# Revit family: Hager-GOLF-Flush_mounted-IP40-With_Cover-With_DIN-Hosted-ES-es
name_source: partatom
category: Electrical Equipment
units: mm (PartAtom-declared; Revit-internal decimal feet)

## family parameters
Cut with Voids When Loaded = No
Host = Face
Maintain Annotation Orientation = Yes
Panel Configuration = Two Columns, Circuits Across
Part Type = Panelboard
Room Calculation Point = No
Round Connector Dimension = Use Diameter
Shared = No

## types (69) — shared parameters
BC_MODEL_ID = 1539129
BC_OBJECT_ID = 512266
BC_OBJECT_VERSION = #7
Code hager = ADD-EC000214_EU
EF000003 - Método de montaje = Montado empotrado (escayola)
EF000007 - Color = Blanco
EF000024 - Resistente a UV = No
EF000049 - Profundidad = 97 mm  [stored 0.318241 ft]
EF000116 - Número RAL = 9010
EF000118 - Con placa de montaje = No
EF000218 - Profundidad de instalación = 72 mm  [stored 0.23622 ft]
EF001062 - Versión de CEM = No
EF001134 - Carril DIN = Yes
EF004462 - Tipo de cierre = Otros
EF005474 - Grado de protección (IP) = IP40
EF006306 - Con candado = No
EF009212 - Versión de la cubierta = Cerrado
ETIM class code = EC000214
ETIM class name = Small distribution board
HG000001 - Número de columnas = 1
HG000002-with door or cover-es = Yes
HG000003-Range-es = GOLF
HG000005-Thickness-es = 2 mm  [stored 0.00656168 ft]
HG000006-Flush mounted-es = Yes
HG000009-Double swing door-es = No
HG000010-Asymmetric doors-es = No
HG000011-Empty rows from bottom-es = No
HG000012-Door swing angle-es = 90.00°
HG000013-Door on the left-es = No
HG000014-Door on the right-es = Yes
HG000015-Clearance visibility-es = Yes
HG000016-Door 3D visibility-es = Yes
HG000017-Distance between poles-es = 18 mm  [stored 0.0590551 ft]
HG000060-RAL-number = 9010
HG000099-Onfly Template ID-es-ES = 507532
Manufacturer = Hager
Name = GOLF-Flush_mounted-IP40-With_Cover-With_DIN-ES
Name BIM&CO = Electricity
Name hager = ADD_Enclosures_EC000214
Uniformat = Low Tension Service & Dist.
Uniformat code = D501001
zero-valued in all types: Default Elevation, EF001131 - Profundidad interna, HG000007-Number of empty columns-es, HG000008-Number of empty rows-es

## per-type parameters (varying)
| type | BC_VARIANT_ID | EF000008 - Anchura | EF000040 - Altura | EF000266 - Número de filas | EF000332 - Altura de la instalación | EF000846 - Anchura de montaje | EF001088 - Posibilidad de extensión | EF002950 - Ancho en número de espacios modulares | EF006244 - Tapa/puerta transparente | EF015776 - Borne de tierra | EF015777 - Borne neutro | EF015941 - Puerta de transmisión de señal | HG000004-Manufacturer reference-es | HGEF000266-Número de filas | HGEF0002950-Ancho en número de espacios modulares |
| GOLF-Flush_mounted_W204_H225_D97_4_Modular_Spacing-VF104PE | 1169244 | 204 mm | 225 mm  [stored 0.738189 ft] | 1 | 189 mm  [stored 0.620079 ft] | 170 mm  [stored 0.557743 ft] | Yes | 4 | No | Yes | No | Yes | VF104PE | 1 | 4 |
| GOLF-Flush_mounted_W204_H225_D97_4_Modular_Spacing-VF104PEH | 1169258 | 204 mm | 225 mm  [stored 0.738189 ft] | 1 | 189 mm  [stored 0.620079 ft] | 170 mm  [stored 0.557743 ft] | Yes | 4 | No | Yes | No | Yes | VF104PEH | 1 | 4 |
| GOLF-Flush_mounted_W204_H225_D97_4_Modular_Spacing-VF104TE | 1169267 | 204 mm | 225 mm  [stored 0.738189 ft] | 1 | 189 mm  [stored 0.620079 ft] | 170 mm  [stored 0.557743 ft] | Yes | 4 | Yes | Yes | No | Yes | VF104TE | 1 | 4 |
| GOLF-Flush_mounted_W275_H225_D97_8_Modular_Spacing-VF108PE | 1169271 | 275 mm | 225 mm  [stored 0.738189 ft] | 1 | 189 mm  [stored 0.620079 ft] | 242 mm  [stored 0.793963 ft] | Yes | 8 | No | Yes | No | Yes | VF108PE | 1 | 8 |
| GOLF-Flush_mounted_W275_H225_D97_8_Modular_Spacing-VF108PEH | 1169277 | 275 mm | 225 mm  [stored 0.738189 ft] | 1 | 189 mm  [stored 0.620079 ft] | 242 mm  [stored 0.793963 ft] | Yes | 8 | No | Yes | No | Yes | VF108PEH | 1 | 8 |
| GOLF-Flush_mounted_W275_H225_D97_8_Modular_Spacing-VF108TE | 1169281 | 275 mm | 225 mm  [stored 0.738189 ft] | 1 | 189 mm  [stored 0.620079 ft] | 242 mm  [stored 0.793963 ft] | Yes | 8 | Yes | Yes | No | Yes | VF108TE | 1 | 8 |
| GOLF-Flush_mounted_W275_H225_D97_8_Modular_Spacing-VF108TJ | 1169285 | 275 mm | 225 mm  [stored 0.738189 ft] | 1 | 189 mm  [stored 0.620079 ft] | 242 mm  [stored 0.793963 ft] | Yes | 8 | Yes | Yes | Yes | Yes | VF108TJ | 1 | 8 |
| GOLF-Flush_mounted_W352_H293_D97_12_Modular_Spacing-VF112PE | 1169289 | 352 mm  [stored 1.15486 ft] | 293 mm | 1 | 257 mm  [stored 0.843176 ft] | 318 mm  [stored 1.04331 ft] | Yes | 12 | No | Yes | No | Yes | VF112PE | 1 | 12 |
| GOLF-Flush_mounted_W352_H293_D97_12_Modular_Spacing-VF112PEH | 1169292 | 352 mm  [stored 1.15486 ft] | 293 mm | 1 | 257 mm  [stored 0.843176 ft] | 318 mm  [stored 1.04331 ft] | Yes | 12 | No | Yes | No | Yes | VF112PEH | 1 | 12 |
| GOLF-Flush_mounted_W352_H293_D97_12_Modular_Spacing-VF112PJ | 1169296 | 352 mm  [stored 1.15486 ft] | 293 mm | 1 | 257 mm  [stored 0.843176 ft] | 318 mm  [stored 1.04331 ft] | Yes | 12 | No | Yes | Yes | Yes | VF112PJ | 1 | 12 |
| GOLF-Flush_mounted_W352_H293_D97_12_Modular_Spacing-VF112PY | 1169299 | 352 mm  [stored 1.15486 ft] | 293 mm | 1 | 257 mm  [stored 0.843176 ft] | 318 mm  [stored 1.04331 ft] | Yes | 12 | No | No | No | No | VF112PY | 1 | 12 |
| GOLF-Flush_mounted_W352_H293_D97_12_Modular_Spacing-VF112TE | 1169302 | 352 mm  [stored 1.15486 ft] | 293 mm | 1 | 257 mm  [stored 0.843176 ft] | 318 mm  [stored 1.04331 ft] | Yes | 12 | Yes | Yes | No | Yes | VF112TE | 1 | 12 |
| GOLF-Flush_mounted_W352_H293_D97_12_Modular_Spacing-VF112TF | 1169305 | 352 mm  [stored 1.15486 ft] | 293 mm | 1 | 257 mm  [stored 0.843176 ft] | 318 mm  [stored 1.04331 ft] | Yes | 12 | Yes | Yes | No | Yes | VF112TF | 1 | 12 |
| GOLF-Flush_mounted_W352_H293_D97_12_Modular_Spacing-VF112TJ | 1169308 | 352 mm  [stored 1.15486 ft] | 293 mm | 1 | 257 mm  [stored 0.843176 ft] | 318 mm  [stored 1.04331 ft] | Yes | 12 | Yes | Yes | Yes | Yes | VF112TJ | 1 | 12 |
| GOLF-Flush_mounted_W352_H293_D97_12_Modular_Spacing-VF112TY | 1169310 | 352 mm  [stored 1.15486 ft] | 293 mm | 1 | 257 mm  [stored 0.843176 ft] | 318 mm  [stored 1.04331 ft] | Yes | 12 | Yes | Yes | Yes | Yes | VF112TY | 1 | 12 |
| GOLF-Flush_mounted_W460_H293_D97_18_Modular_Spacing-VF118PEH | 1169312 | 460 mm  [stored 1.50919 ft] | 293 mm | 1 | 257 mm  [stored 0.843176 ft] | 426 mm  [stored 1.39764 ft] | Yes | 18 | No | Yes | No | Yes | VF118PEH | 1 | 18 |
| GOLF-Flush_mounted_W460_H293_D97_18_Modular_Spacing-VF118PES | 1169314 | 460 mm  [stored 1.50919 ft] | 293 mm | 1 | 257 mm  [stored 0.843176 ft] | 426 mm  [stored 1.39764 ft] | Yes | 18 | No | No | No | Yes | VF118PES | 1 | 18 |
| GOLF-Flush_mounted_W460_H293_D97_18_Modular_Spacing-VF118PJ | 1169316 | 460 mm  [stored 1.50919 ft] | 293 mm | 1 | 257 mm  [stored 0.843176 ft] | 426 mm  [stored 1.39764 ft] | Yes | 18 | No | Yes | Yes | Yes | VF118PJ | 1 | 18 |
| GOLF-Flush_mounted_W460_H293_D97_18_Modular_Spacing-VF118PY | 1169318 | 460 mm  [stored 1.50919 ft] | 293 mm | 1 | 257 mm  [stored 0.843176 ft] | 426 mm  [stored 1.39764 ft] | Yes | 18 | No | Yes | Yes | Yes | VF118PY | 1 | 18 |
| GOLF-Flush_mounted_W460_H293_D97_18_Modular_Spacing-VF118TES | 1169320 | 460 mm  [stored 1.50919 ft] | 293 mm | 1 | 257 mm  [stored 0.843176 ft] | 426 mm  [stored 1.39764 ft] | Yes | 18 | Yes | No | No | Yes | VF118TES | 1 | 18 |
| GOLF-Flush_mounted_W460_H293_D97_18_Modular_Spacing-VF118TF | 1169322 | 460 mm  [stored 1.50919 ft] | 293 mm | 1 | 257 mm  [stored 0.843176 ft] | 426 mm  [stored 1.39764 ft] | Yes | 18 | Yes | Yes | No | Yes | VF118TF | 1 | 18 |
| GOLF-Flush_mounted_W460_H293_D97_18_Modular_Spacing-VF118TJ | 1169324 | 460 mm  [stored 1.50919 ft] | 293 mm | 1 | 257 mm  [stored 0.843176 ft] | 426 mm  [stored 1.39764 ft] | Yes | 18 | Yes | Yes | Yes | Yes | VF118TJ | 1 | 18 |
| GOLF-Flush_mounted_W532_H293_D97_22_Modular_Spacing-VF122PJ | 1169326 | 532 mm  [stored 1.74541 ft] | 293 mm | 1 | 257 mm  [stored 0.843176 ft] | 498 mm  [stored 1.63386 ft] | Yes | 22 | No | Yes | Yes | Yes | VF122PJ | 1 | 22 |
| GOLF-Flush_mounted_W532_H293_D97_22_Modular_Spacing-VF122PY | 1169328 | 532 mm  [stored 1.74541 ft] | 293 mm | 1 | 257 mm  [stored 0.843176 ft] | 498 mm  [stored 1.63386 ft] | Yes | 22 | No | Yes | Yes | Yes | VF122PY | 1 | 22 |
| GOLF-Flush_mounted_W532_H293_D97_22_Modular_Spacing-VF122TJ | 1169330 | 532 mm  [stored 1.74541 ft] | 293 mm | 1 | 257 mm  [stored 0.843176 ft] | 498 mm  [stored 1.63386 ft] | Yes | 22 | Yes | Yes | Yes | Yes | VF122TJ | 1 | 22 |
| GOLF-Flush_mounted_W382_H418_D97_12_Modular_Spacing-VF212PE | 1169332 | 382 mm  [stored 1.25328 ft] | 418 mm  [stored 1.37139 ft] | 2 | 382 mm  [stored 1.25328 ft] | 318 mm  [stored 1.04331 ft] | Yes | 12 | No | Yes | No | Yes | VF212PE | 2 | 12 |
| GOLF-Flush_mounted_W382_H418_D97_12_Modular_Spacing-VF212PEH | 1169333 | 382 mm  [stored 1.25328 ft] | 418 mm  [stored 1.37139 ft] | 2 | 382 mm  [stored 1.25328 ft] | 318 mm  [stored 1.04331 ft] | Yes | 12 | No | Yes | No | Yes | VF212PEH | 2 | 12 |
| GOLF-Flush_mounted_W382_H418_D97_12_Modular_Spacing-VF212PJ | 1169335 | 382 mm  [stored 1.25328 ft] | 418 mm  [stored 1.37139 ft] | 2 | 382 mm  [stored 1.25328 ft] | 318 mm  [stored 1.04331 ft] | Yes | 12 | No | Yes | Yes | Yes | VF212PJ | 2 | 12 |
| GOLF-Flush_mounted_W382_H418_D97_12_Modular_Spacing-VF212PY | 1169337 | 382 mm  [stored 1.25328 ft] | 418 mm  [stored 1.37139 ft] | 2 | 382 mm  [stored 1.25328 ft] | 318 mm  [stored 1.04331 ft] | Yes | 12 | No | Yes | Yes | Yes | VF212PY | 2 | 12 |
| GOLF-Flush_mounted_W382_H418_D97_12_Modular_Spacing-VF212TE | 1169339 | 382 mm  [stored 1.25328 ft] | 418 mm  [stored 1.37139 ft] | 2 | 382 mm  [stored 1.25328 ft] | 318 mm  [stored 1.04331 ft] | Yes | 12 | Yes | Yes | No | Yes | VF212TE | 2 | 12 |
| GOLF-Flush_mounted_W382_H418_D97_12_Modular_Spacing-VF212TF | 1169341 | 382 mm  [stored 1.25328 ft] | 418 mm  [stored 1.37139 ft] | 2 | 382 mm  [stored 1.25328 ft] | 318 mm  [stored 1.04331 ft] | Yes | 12 | Yes | Yes | No | Yes | VF212TF | 2 | 12 |
| GOLF-Flush_mounted_W382_H418_D97_12_Modular_Spacing-VF212TJ | 1169342 | 382 mm  [stored 1.25328 ft] | 418 mm  [stored 1.37139 ft] | 2 | 382 mm  [stored 1.25328 ft] | 318 mm  [stored 1.04331 ft] | Yes | 12 | Yes | Yes | Yes | Yes | VF212TJ | 2 | 12 |
| GOLF-Flush_mounted_W382_H418_D97_12_Modular_Spacing-VF212TY | 1169344 | 382 mm  [stored 1.25328 ft] | 418 mm  [stored 1.37139 ft] | 2 | 382 mm  [stored 1.25328 ft] | 318 mm  [stored 1.04331 ft] | Yes | 12 | Yes | Yes | Yes | Yes | VF212TY | 2 | 12 |
| GOLF-Flush_mounted_W460_H418_D97_18_Modular_Spacing-VF218PEH | 1169346 | 460 mm  [stored 1.50919 ft] | 418 mm  [stored 1.37139 ft] | 2 | 382 mm  [stored 1.25328 ft] | 426 mm  [stored 1.39764 ft] | Yes | 18 | No | Yes | No | Yes | VF218PEH | 2 | 18 |
| GOLF-Flush_mounted_W460_H418_D97_18_Modular_Spacing-VF218PES | 1169347 | 460 mm  [stored 1.50919 ft] | 418 mm  [stored 1.37139 ft] | 2 | 382 mm  [stored 1.25328 ft] | 426 mm  [stored 1.39764 ft] | Yes | 18 | No | No | No | Yes | VF218PES | 2 | 18 |
| GOLF-Flush_mounted_W460_H418_D97_18_Modular_Spacing-VF218PF | 1169348 | 460 mm  [stored 1.50919 ft] | 418 mm  [stored 1.37139 ft] | 2 | 382 mm  [stored 1.25328 ft] | 426 mm  [stored 1.39764 ft] | Yes | 18 | No | Yes | No | Yes | VF218PF | 2 | 18 |
| GOLF-Flush_mounted_W460_H418_D97_18_Modular_Spacing-VF218PJ | 1169349 | 460 mm  [stored 1.50919 ft] | 418 mm  [stored 1.37139 ft] | 2 | 382 mm  [stored 1.25328 ft] | 426 mm  [stored 1.39764 ft] | Yes | 18 | No | Yes | Yes | Yes | VF218PJ | 2 | 18 |
| GOLF-Flush_mounted_W460_H418_D97_18_Modular_Spacing-VF218PY | 1169350 | 460 mm  [stored 1.50919 ft] | 418 mm  [stored 1.37139 ft] | 2 | 382 mm  [stored 1.25328 ft] | 426 mm  [stored 1.39764 ft] | Yes | 18 | No | Yes | Yes | Yes | VF218PY | 2 | 18 |
| GOLF-Flush_mounted_W460_H418_D97_18_Modular_Spacing-VF218TES | 1169351 | 460 mm  [stored 1.50919 ft] | 418 mm  [stored 1.37139 ft] | 2 | 382 mm  [stored 1.25328 ft] | 426 mm  [stored 1.39764 ft] | Yes | 18 | Yes | No | No | Yes | VF218TES | 2 | 18 |
| GOLF-Flush_mounted_W460_H418_D97_18_Modular_Spacing-VF218TF | 1169352 | 460 mm  [stored 1.50919 ft] | 418 mm  [stored 1.37139 ft] | 2 | 382 mm  [stored 1.25328 ft] | 426 mm  [stored 1.39764 ft] | No | 18 | No | No | No | No | VF218TF | 2 | 18 |
| GOLF-Flush_mounted_W460_H418_D97_18_Modular_Spacing-VF218TJ | 1169353 | 460 mm  [stored 1.50919 ft] | 418 mm  [stored 1.37139 ft] | 2 | 382 mm  [stored 1.25328 ft] | 426 mm  [stored 1.39764 ft] | Yes | 18 | Yes | Yes | Yes | Yes | VF218TJ | 2 | 18 |
| GOLF-Flush_mounted_W352_H543_D97_12_Modular_Spacing-VF312ICT | 1169354 | 352 mm  [stored 1.15486 ft] | 543 mm  [stored 1.7815 ft] | 3 | 507 mm  [stored 1.66339 ft] | 318 mm  [stored 1.04331 ft] | Yes | 12 | No | No | No | Yes | VF312ICT | 3 | 12 |
| GOLF-Flush_mounted_W352_H543_D97_12_Modular_Spacing-VF312PE | 1169355 | 352 mm  [stored 1.15486 ft] | 543 mm  [stored 1.7815 ft] | 3 | 507 mm  [stored 1.66339 ft] | 318 mm  [stored 1.04331 ft] | Yes | 12 | No | Yes | No | Yes | VF312PE | 3 | 12 |
| GOLF-Flush_mounted_W352_H543_D97_12_Modular_Spacing-VF312PEH | 1169356 | 352 mm  [stored 1.15486 ft] | 543 mm  [stored 1.7815 ft] | 3 | 507 mm  [stored 1.66339 ft] | 318 mm  [stored 1.04331 ft] | Yes | 12 | No | Yes | No | Yes | VF312PEH | 3 | 12 |
| GOLF-Flush_mounted_W352_H543_D97_12_Modular_Spacing-VF312PJ | 1169357 | 352 mm  [stored 1.15486 ft] | 543 mm  [stored 1.7815 ft] | 3 | 507 mm  [stored 1.66339 ft] | 318 mm  [stored 1.04331 ft] | Yes | 12 | No | Yes | Yes | Yes | VF312PJ | 3 | 12 |
| GOLF-Flush_mounted_W352_H543_D97_12_Modular_Spacing-VF312PY | 1169358 | 352 mm  [stored 1.15486 ft] | 543 mm  [stored 1.7815 ft] | 3 | 507 mm  [stored 1.66339 ft] | 318 mm  [stored 1.04331 ft] | Yes | 12 | No | Yes | Yes | Yes | VF312PY | 3 | 12 |
| GOLF-Flush_mounted_W352_H543_D97_12_Modular_Spacing-VF312TE | 1169359 | 352 mm  [stored 1.15486 ft] | 543 mm  [stored 1.7815 ft] | 3 | 507 mm  [stored 1.66339 ft] | 318 mm  [stored 1.04331 ft] | Yes | 12 | Yes | Yes | No | Yes | VF312TE | 3 | 12 |
| GOLF-Flush_mounted_W352_H543_D97_12_Modular_Spacing-VF312TF | 1169360 | 352 mm  [stored 1.15486 ft] | 543 mm  [stored 1.7815 ft] | 3 | 507 mm  [stored 1.66339 ft] | 318 mm  [stored 1.04331 ft] | Yes | 12 | Yes | Yes | No | Yes | VF312TF | 3 | 12 |
| GOLF-Flush_mounted_W352_H543_D97_12_Modular_Spacing-VF312TJ | 1169361 | 352 mm  [stored 1.15486 ft] | 543 mm  [stored 1.7815 ft] | 3 | 507 mm  [stored 1.66339 ft] | 318 mm  [stored 1.04331 ft] | Yes | 12 | Yes | Yes | Yes | Yes | VF312TJ | 3 | 12 |
| GOLF-Flush_mounted_W352_H543_D97_12_Modular_Spacing-VF312TY | 1169362 | 352 mm  [stored 1.15486 ft] | 543 mm  [stored 1.7815 ft] | 3 | 507 mm  [stored 1.66339 ft] | 318 mm  [stored 1.04331 ft] | Yes | 12 | Yes | Yes | Yes | Yes | VF312TY | 3 | 12 |
| GOLF-Flush_mounted_W460_H543_D97_18_Modular_Spacing-VF318PEH | 1169363 | 460 mm  [stored 1.50919 ft] | 543 mm  [stored 1.7815 ft] | 3 | 507 mm  [stored 1.66339 ft] | 426 mm  [stored 1.39764 ft] | Yes | 18 | No | Yes | No | Yes | VF318PEH | 3 | 18 |
| GOLF-Flush_mounted_W460_H543_D97_18_Modular_Spacing-VF318PES | 1169364 | 460 mm  [stored 1.50919 ft] | 543 mm  [stored 1.7815 ft] | 3 | 507 mm  [stored 1.66339 ft] | 426 mm  [stored 1.39764 ft] | Yes | 18 | No | No | No | Yes | VF318PES | 3 | 18 |
| GOLF-Flush_mounted_W460_H543_D97_18_Modular_Spacing-VF318PJ | 1169365 | 460 mm  [stored 1.50919 ft] | 543 mm  [stored 1.7815 ft] | 3 | 507 mm  [stored 1.66339 ft] | 426 mm  [stored 1.39764 ft] | Yes | 18 | No | Yes | Yes | Yes | VF318PJ | 3 | 18 |
| GOLF-Flush_mounted_W460_H543_D97_18_Modular_Spacing-VF318PY | 1169366 | 460 mm  [stored 1.50919 ft] | 543 mm  [stored 1.7815 ft] | 3 | 507 mm  [stored 1.66339 ft] | 426 mm  [stored 1.39764 ft] | Yes | 18 | No | Yes | Yes | Yes | VF318PY | 3 | 18 |
| GOLF-Flush_mounted_W460_H543_D97_18_Modular_Spacing-VF318TES | 1169367 | 460 mm  [stored 1.50919 ft] | 543 mm  [stored 1.7815 ft] | 3 | 507 mm  [stored 1.66339 ft] | 426 mm  [stored 1.39764 ft] | Yes | 18 | Yes | No | No | Yes | VF318TES | 3 | 18 |
| GOLF-Flush_mounted_W460_H543_D97_18_Modular_Spacing-VF318TJ | 1169368 | 460 mm  [stored 1.50919 ft] | 543 mm  [stored 1.7815 ft] | 3 | 507 mm  [stored 1.66339 ft] | 426 mm  [stored 1.39764 ft] | Yes | 18 | Yes | Yes | Yes | Yes | VF318TJ | 3 | 18 |
| GOLF-Flush_mounted_W352_H688_D97_12_Modular_Spacing-VF412PE | 1169369 | 352 mm  [stored 1.15486 ft] | 688 mm  [stored 2.25722 ft] | 4 | 652 mm  [stored 2.13911 ft] | 318 mm  [stored 1.04331 ft] | Yes | 12 | No | Yes | No | Yes | VF412PE | 4 | 12 |
| GOLF-Flush_mounted_W352_H688_D97_12_Modular_Spacing-VF412PEH | 1169370 | 352 mm  [stored 1.15486 ft] | 688 mm  [stored 2.25722 ft] | 4 | 652 mm  [stored 2.13911 ft] | 318 mm  [stored 1.04331 ft] | Yes | 12 | No | Yes | No | Yes | VF412PEH | 4 | 12 |
| GOLF-Flush_mounted_W352_H688_D97_12_Modular_Spacing-VF412PJ | 1169371 | 352 mm  [stored 1.15486 ft] | 688 mm  [stored 2.25722 ft] | 4 | 652 mm  [stored 2.13911 ft] | 318 mm  [stored 1.04331 ft] | Yes | 12 | No | Yes | Yes | Yes | VF412PJ | 4 | 12 |
| GOLF-Flush_mounted_W352_H688_D97_12_Modular_Spacing-VF412PY | 1169372 | 352 mm  [stored 1.15486 ft] | 688 mm  [stored 2.25722 ft] | 4 | 652 mm  [stored 2.13911 ft] | 318 mm  [stored 1.04331 ft] | Yes | 12 | No | Yes | Yes | Yes | VF412PY | 4 | 12 |
| GOLF-Flush_mounted_W352_H688_D97_12_Modular_Spacing-VF412TE | 1169373 | 352 mm  [stored 1.15486 ft] | 688 mm  [stored 2.25722 ft] | 4 | 652 mm  [stored 2.13911 ft] | 318 mm  [stored 1.04331 ft] | Yes | 12 | Yes | Yes | No | Yes | VF412TE | 4 | 12 |
| GOLF-Flush_mounted_W352_H688_D97_12_Modular_Spacing-VF412TJ | 1169374 | 352 mm  [stored 1.15486 ft] | 688 mm  [stored 2.25722 ft] | 4 | 652 mm  [stored 2.13911 ft] | 318 mm  [stored 1.04331 ft] | Yes | 12 | Yes | Yes | Yes | Yes | VF412TJ | 4 | 12 |
| GOLF-Flush_mounted_W460_H688_D97_18_Modular_Spacing-VF418PEH | 1169375 | 460 mm  [stored 1.50919 ft] | 688 mm  [stored 2.25722 ft] | 4 | 652 mm  [stored 2.13911 ft] | 426 mm  [stored 1.39764 ft] | Yes | 18 | No | Yes | No | Yes | VF418PEH | 4 | 18 |
| GOLF-Flush_mounted_W460_H688_D97_18_Modular_Spacing-VF418PES | 1169376 | 460 mm  [stored 1.50919 ft] | 688 mm  [stored 2.25722 ft] | 4 | 652 mm  [stored 2.13911 ft] | 426 mm  [stored 1.39764 ft] | Yes | 18 | No | No | No | Yes | VF418PES | 4 | 18 |
| GOLF-Flush_mounted_W460_H688_D97_18_Modular_Spacing-VF418PJ | 1169377 | 460 mm  [stored 1.50919 ft] | 688 mm  [stored 2.25722 ft] | 4 | 652 mm  [stored 2.13911 ft] | 426 mm  [stored 1.39764 ft] | Yes | 18 | No | Yes | Yes | Yes | VF418PJ | 4 | 18 |
| GOLF-Flush_mounted_W460_H688_D97_18_Modular_Spacing-VF418PY | 1169378 | 460 mm  [stored 1.50919 ft] | 688 mm  [stored 2.25722 ft] | 4 | 652 mm  [stored 2.13911 ft] | 426 mm  [stored 1.39764 ft] | Yes | 18 | No | Yes | Yes | Yes | VF418PY | 4 | 18 |
| GOLF-Flush_mounted_W460_H688_D97_18_Modular_Spacing-VF418TES | 1169379 | 460 mm  [stored 1.50919 ft] | 688 mm  [stored 2.25722 ft] | 4 | 652 mm  [stored 2.13911 ft] | 426 mm  [stored 1.39764 ft] | Yes | 18 | Yes | No | No | Yes | VF418TES | 4 | 18 |
| GOLF-Flush_mounted_W460_H688_D97_18_Modular_Spacing-VF418TF | 1169380 | 460 mm  [stored 1.50919 ft] | 688 mm  [stored 2.25722 ft] | 4 | 652 mm  [stored 2.13911 ft] | 426 mm  [stored 1.39764 ft] | Yes | 18 | Yes | Yes | No | Yes | VF418TF | 4 | 18 |
| GOLF-Flush_mounted_W460_H688_D97_18_Modular_Spacing-VF418TJ | 1169381 | 460 mm  [stored 1.50919 ft] | 688 mm  [stored 2.25722 ft] | 4 | 652 mm  [stored 2.13911 ft] | 426 mm  [stored 1.39764 ft] | Yes | 18 | Yes | Yes | Yes | Yes | VF418TJ | 4 | 18 |

note: column(s) folded — value = type name in every type: Reference

note: [stored X ft] marks values corroborated as IEEE doubles in the binary element streams (Revit-internal decimal feet)

## geometry (parser evidence)
native form markers: Sweep x16
no freeform markers — native parametric forms only
